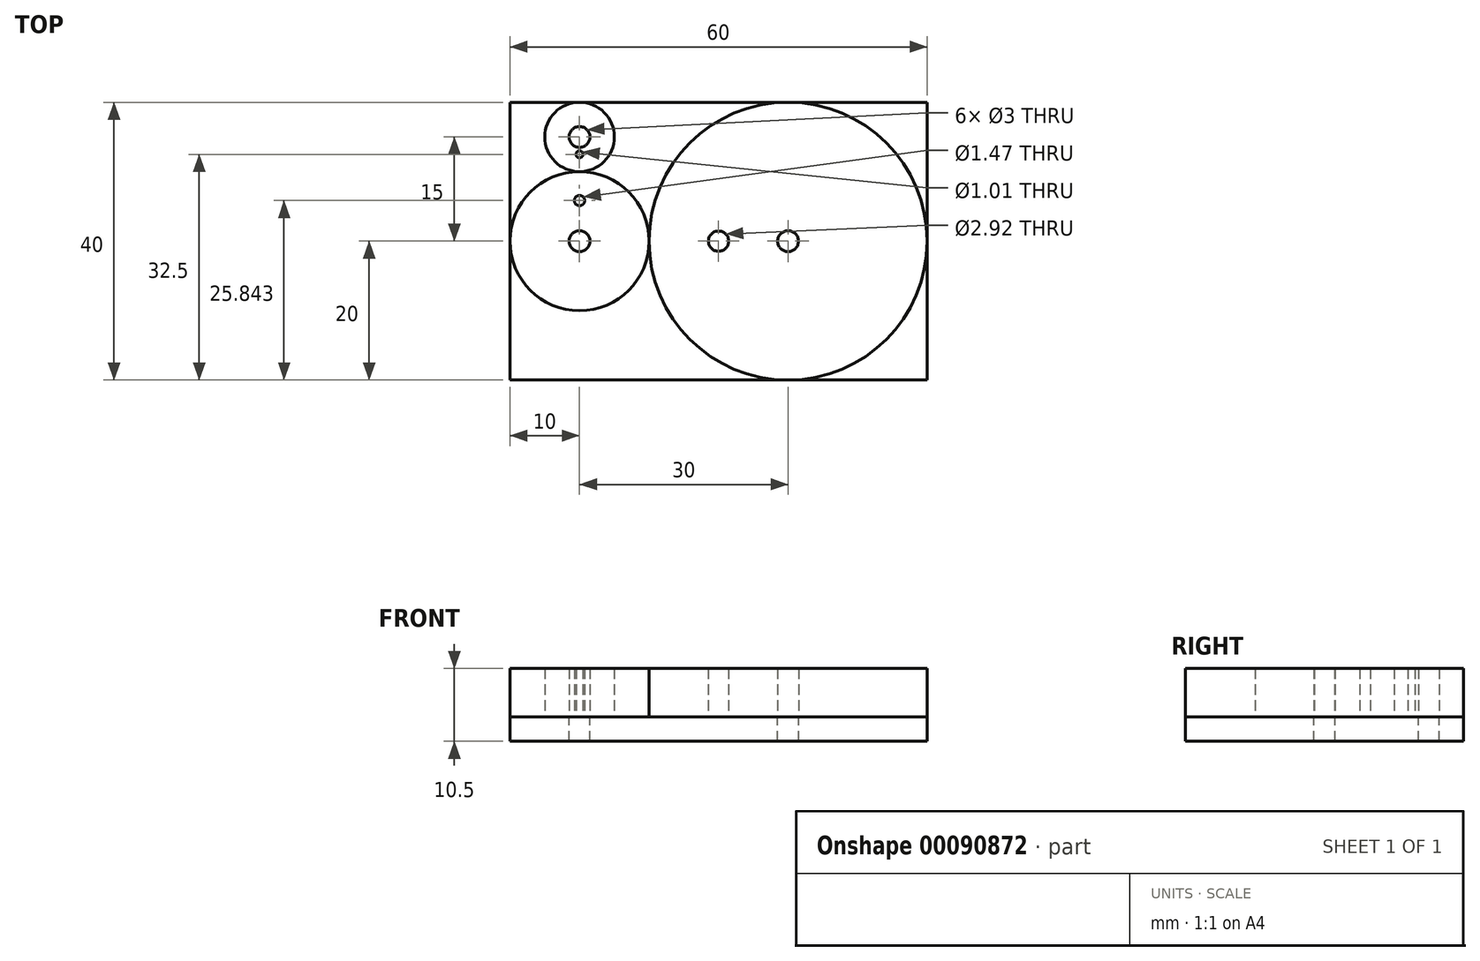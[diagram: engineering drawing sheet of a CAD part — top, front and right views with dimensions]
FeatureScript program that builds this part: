
annotation { "Feature Type Name" : "Feature", "Feature Type Description" : "" }
export const myFeature = defineFeature(function(context is Context, id is Id, definition is map)
    precondition{}
    {
        {
            var Q0;
            Q0=qCreatedBy(makeId("Top.planeOp"),FACE);
            var sketch = newSketch(context, id + "F0", { "sketchPlane" : qUnion([Q0])});
            skLineSegment(sketch, "E0.right", {"start": v(30, 20) * mm, "end": v(30, -20) * mm});
            skPoint(sketch, "E0.middle", {"position": v(0, 0) * mm});
            skCircle(sketch, "E1", {"center": v(0, 0) * mm, "radius": 10 * mm});
            skLineSegment(sketch, "E2", {"start": v(10, 0) * mm, "end": v(30, 0) * mm, "construction": true});
            skCircle(sketch, "E3", {"center": v(30, 0) * mm, "radius": 20 * mm});
            skLineSegment(sketch, "E4", {"start": v(0, 10) * mm, "end": v(0, 15) * mm, "construction": true});
            skCircle(sketch, "E5", {"center": v(0, 15) * mm, "radius": 5 * mm});
            skLineSegment(sketch, "E6", {"start": v(-10, 0) * mm, "end": v(-10, -20) * mm, "construction": true});
            skLineSegment(sketch, "E7", {"start": v(50, 0) * mm, "end": v(50, 20) * mm, "construction": true});
            skLineSegment(sketch, "E8.bottom", {"start": v(-10, -20) * mm, "end": v(50, -20) * mm});
            skLineSegment(sketch, "E8.top", {"start": v(-10, 20) * mm, "end": v(50, 20) * mm});
            skLineSegment(sketch, "E8.left", {"start": v(-10, -20) * mm, "end": v(-10, 20) * mm});
            skLineSegment(sketch, "E8.right", {"start": v(50, -20) * mm, "end": v(50, 20) * mm});
            skPoint(sketch, "E0.bottom.start.orphan", {"position": v(-30, 30) * mm});
            skPoint(sketch, "E0.top.start.orphan", {"position": v(-30, -30) * mm});
            skPoint(sketch, "E9.orphan", {"position": v(30, -30) * mm});
            skPoint(sketch, "E10.orphan", {"position": v(30, 30) * mm});
            skCircle(sketch, "E11", {"center": v(30, 0) * mm, "radius": 1.5 * mm});
            skCircle(sketch, "E12", {"center": v(0, 0) * mm, "radius": 1.5 * mm});
            skCircle(sketch, "E13", {"center": v(0, 15) * mm, "radius": 1.5 * mm});
            skCircle(sketch, "E14", {"center": v(20, 0) * mm, "radius": 1.46 * mm});
            skCircle(sketch, "E15", {"center": v(0, 5.84) * mm, "radius": 0.74 * mm});
            skCircle(sketch, "E16", {"center": v(0, 12.5) * mm, "radius": 0.5 * mm});
            skSolve(sketch);
        }
        {
            var Q0;
            {var subQ1=sQuery(id+"F0.wireOp",EDGE,"E0.right");var subQ4=sQuery(id+"F0.wireOp",EDGE,"E11");var subQ5=makeQuery(id+"F0.imprint","INTERSECT",VERTEX,{"disambiguationData":[OD(0.0)],"derivedFrom":[subQ1,subQ4]});Q0=makeQuery(id+"F0.imprint","IMPRINT",FACE,{"disambiguationData":[TD([[makeQuery(id+"F0.imprint","IMPRINT",EDGE,{"disambiguationData":[TD([[subQ5,-1.0]])],"derivedFrom":subQ4}),-1.0]])]});}
            var Q1;
            {var subQ1=sQuery(id+"F0.wireOp",EDGE,"E0.right");var subQ4=sQuery(id+"F0.wireOp",EDGE,"E11");var subQ6=makeQuery(id+"F0.imprint","INTERSECT",VERTEX,{"disambiguationData":[OD(0.0)],"derivedFrom":[subQ1,subQ4]});Q1=makeQuery(id+"F0.imprint","IMPRINT",FACE,{"disambiguationData":[TD([[makeQuery(id+"F0.imprint","IMPRINT",EDGE,{"disambiguationData":[TD([[subQ6,1.0]])],"derivedFrom":subQ4}),-1.0]])]});}
            extrude(context, id + "F1", {"entities" : qUnion([Q0, Q1]), "depth" : 7 * mm});
        }
        {
            var Q0;
            Q0=makeQuery(id+"F0.imprint","IMPRINT",FACE,{"disambiguationData":[TD([[makeQuery(id+"F0.imprint","IMPRINT",EDGE,{"derivedFrom":sQuery(id+"F0.wireOp",EDGE,"E12")}),-1.0]])]});
            extrude(context, id + "F2", {"entities" : qUnion([Q0]), "depth" : 7 * mm});
        }
        {
            var Q0;
            Q0=makeQuery(id+"F0.imprint","IMPRINT",FACE,{"disambiguationData":[TD([[makeQuery(id+"F0.imprint","IMPRINT",EDGE,{"derivedFrom":sQuery(id+"F0.wireOp",EDGE,"E13")}),-1.0]])]});
            extrude(context, id + "F3", {"entities" : qUnion([Q0]), "depth" : 7 * mm});
        }
        {
            var Q0;
            Q0=qCreatedBy(makeId("Top.planeOp"),FACE);
            var sketch = newSketch(context, id + "F4", { "sketchPlane" : qUnion([Q0])});
            skLineSegment(sketch, "E17", {"start": v(0, 0) * mm, "end": v(-10, 0) * mm, "construction": true});
            skLineSegment(sketch, "E18", {"start": v(-10, 0) * mm, "end": v(-10, 20) * mm, "construction": true});
            skLineSegment(sketch, "E19.bottom", {"start": v(-10, 20) * mm, "end": v(50, 20) * mm});
            skLineSegment(sketch, "E19.top", {"start": v(-10, -20) * mm, "end": v(50, -20) * mm});
            skLineSegment(sketch, "E19.left", {"start": v(-10, 20) * mm, "end": v(-10, -20) * mm});
            skLineSegment(sketch, "E19.right", {"start": v(50, 20) * mm, "end": v(50, -20) * mm});
            skCircle(sketch, "E20", {"center": v(0, 0) * mm, "radius": 1.5 * mm});
            skLineSegment(sketch, "E21", {"start": v(0, 0) * mm, "end": v(0, 15) * mm, "construction": true});
            skCircle(sketch, "E22", {"center": v(0, 15) * mm, "radius": 1.5 * mm});
            skLineSegment(sketch, "E23", {"start": v(0, 0) * mm, "end": v(30, 0) * mm, "construction": true});
            skCircle(sketch, "E24", {"center": v(30, 0) * mm, "radius": 1.5 * mm});
            skSolve(sketch);
        }
        {
            var Q0;
            Q0=makeQuery(id+"F4.imprint","IMPRINT",FACE,{"disambiguationData":[TD([[makeQuery(id+"F4.imprint","IMPRINT",EDGE,{"derivedFrom":sQuery(id+"F4.wireOp",EDGE,"E19.bottom")}),-1.0]])]});
            extrude(context, id + "F5", {"entities" : qUnion([Q0]), "oppositeDirection" : true, "depth" : 3.5 * mm});
        }
    });
